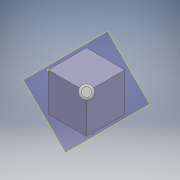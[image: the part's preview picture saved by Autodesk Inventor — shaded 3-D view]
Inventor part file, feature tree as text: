
AUTODESK INVENTOR PART (.ipt)
format: ipt  version: 2018 (Build 220112000, 112)  size: 129,536 bytes
history: native  units: mm
features: sketch x4, extrude x3, plane x2, shell x1, fillet x1, projected_geometry x1
ambient origin geometry x8: Origin, YZ Plane, XZ Plane, XY Plane, X Axis, Y Axis, Z Axis, Center Point
bodies: Solid1 (feature_tree)
feature tree (12):
  extrude  "Extrusion1"  Depth=10.0mm
  shell  "Shell1"  Thickness=10.0mm
  plane  "Work Plane2"
  extrude  "Extrusion2"  Depth=2.0mm
  sketch  "Sketch3"  dims[d6=6.25mm d7=0.0mm d8=4.0mm d9=0.0mm d10=0.5mm]
  extrude  "Extrusion3"  Depth=0.5mm TaperAngle=0.0deg
  fillet  "Fillet1"  Radius=0.5mm
  sketch  "Sketch1"  dims[d0=10.0mm d1=10.0mm d2=10.0mm d3=0.0mm]
  plane  "Work Plane1"
  sketch  "Sketch2"  dims[d4=2.0mm d5=3.0mm]
  sketch  "Sketch4"
  projected_geometry  "Projected Loop1"
